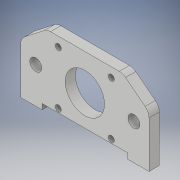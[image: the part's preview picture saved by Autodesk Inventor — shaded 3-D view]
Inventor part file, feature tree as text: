
AUTODESK INVENTOR PART (.ipt)
format: ipt  version: 2019 (Build 230136000, 136)  size: 155,648 bytes
history: native  units: mm
features: extrude x1, fillet x1, sketch x1
ambient origin geometry x8: Origin, YZ Plane, XZ Plane, XY Plane, X Axis, Y Axis, Z Axis, Center Point
bodies: Body1 (feature_tree)
feature tree (3):
  extrude  "Extrusion2"  Depth=42.0mm
  fillet  "Fillet2"  Radius=22.340214mm
  sketch  "Sketch1"  dims[d0=30.0mm d1=30.0mm d3=22.340214mm d4=75.0mm d5=7.0mm d7=7.0mm d9=28.678mm d10=28.678mm d13=3.5mm d14=3.5mm d15=15.5mm d16=15.5mm d21=3.5mm d22=3.5mm d23=31.0mm d24=23.0mm d25=6.0mm d26=0.0mm d27=6.0mm d28=50.0mm d29=12.5mm d30=3.2mm d31=17.8mm d32=2.3mm d33=22.340214mm d34=44.281401mm d35=12.0mm d36=12.0mm d37=42.0mm]
